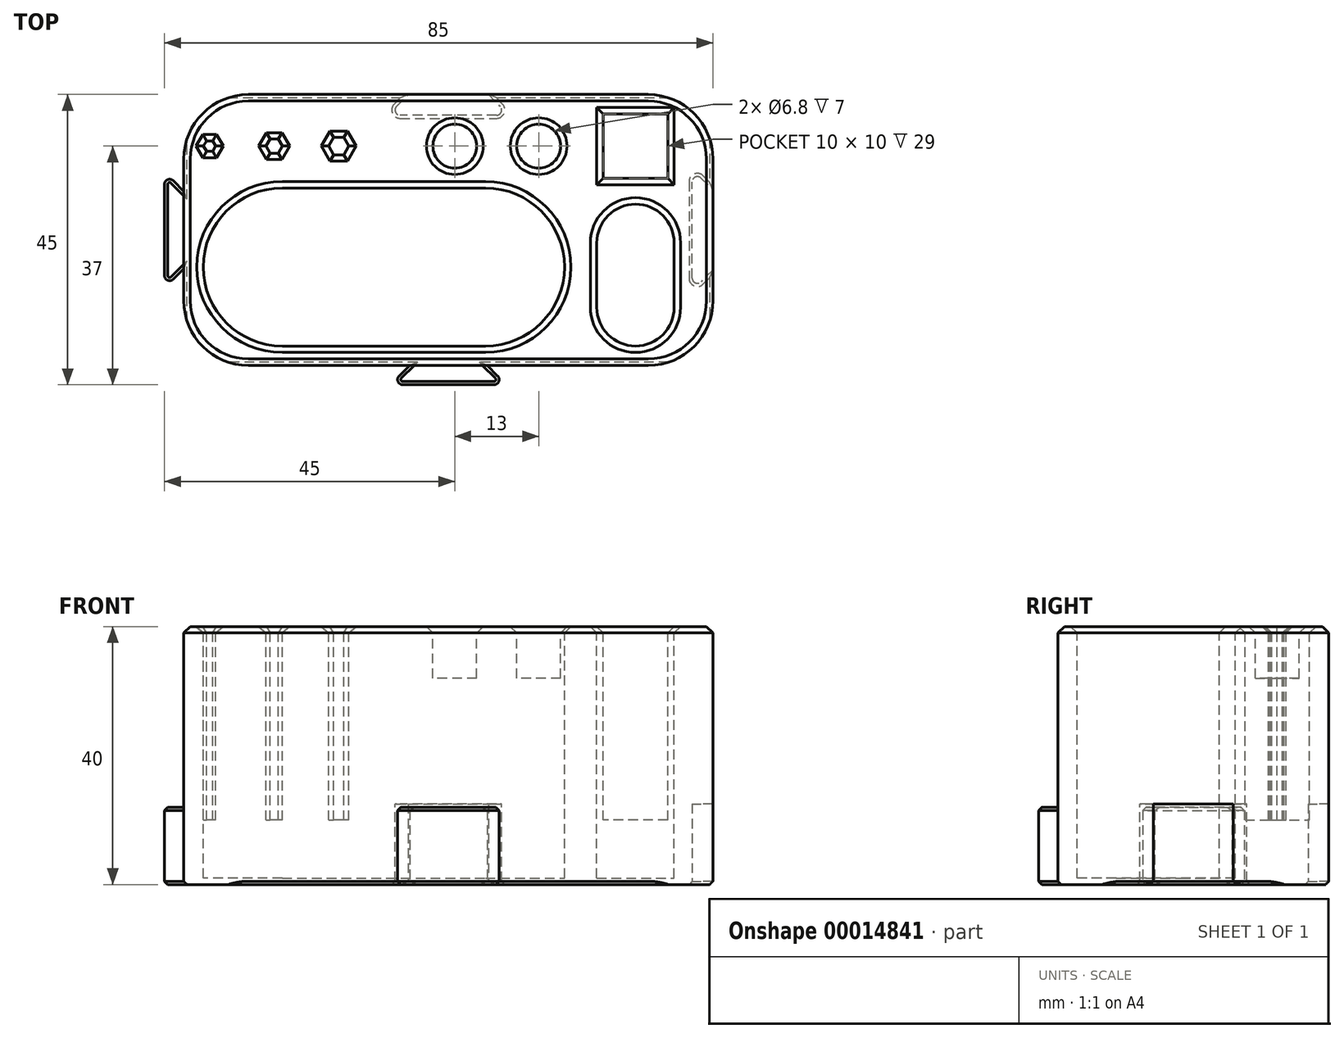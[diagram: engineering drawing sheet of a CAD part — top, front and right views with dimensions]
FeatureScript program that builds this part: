
annotation { "Feature Type Name" : "Feature", "Feature Type Description" : "" }
export const myFeature = defineFeature(function(context is Context, id is Id, definition is map)
    precondition{}
    {
        {
            var Q0;
            Q0=qCreatedBy(makeId("Top.planeOp"),FACE);
            var sketch = newSketch(context, id + "F0", { "sketchPlane" : qUnion([Q0])});
            skLineSegment(sketch, "E0.bottom", {"start": v(0, 0) * mm, "end": v(82, 0) * mm});
            skLineSegment(sketch, "E0.top", {"start": v(0, 42) * mm, "end": v(82, 42) * mm});
            skLineSegment(sketch, "E0.left", {"start": v(0, 0) * mm, "end": v(0, 42) * mm});
            skLineSegment(sketch, "E0.right", {"start": v(82, 0) * mm, "end": v(82, 42) * mm});
            skLineSegment(sketch, "E1", {"start": v(0, 21) * mm, "end": v(82, 21) * mm, "construction": true});
            skLineSegment(sketch, "E2", {"start": v(41, 42) * mm, "end": v(41, 0) * mm, "construction": true});
            skLineSegment(sketch, "E3", {"start": v(35, 0) * mm, "end": v(32, -3) * mm});
            skLineSegment(sketch, "E4", {"start": v(32, -3) * mm, "end": v(50, -3) * mm});
            skLineSegment(sketch, "E5", {"start": v(50, -3) * mm, "end": v(47, 0) * mm});
            skLineSegment(sketch, "E6", {"start": v(47.2, 42) * mm, "end": v(50.4, 38.8) * mm});
            skLineSegment(sketch, "E7", {"start": v(50.4, 38.8) * mm, "end": v(31.6, 38.8) * mm});
            skLineSegment(sketch, "E8", {"start": v(31.6, 38.8) * mm, "end": v(34.8, 42) * mm});
            skLineSegment(sketch, "E9", {"start": v(0, 15) * mm, "end": v(-3, 12) * mm});
            skLineSegment(sketch, "E10", {"start": v(-3, 12) * mm, "end": v(-3, 30) * mm});
            skLineSegment(sketch, "E11", {"start": v(-3, 30) * mm, "end": v(0, 27) * mm});
            skLineSegment(sketch, "E12", {"start": v(82, 14.8) * mm, "end": v(78.8, 11.6) * mm});
            skLineSegment(sketch, "E13", {"start": v(78.8, 11.6) * mm, "end": v(78.8, 30.4) * mm});
            skLineSegment(sketch, "E14", {"start": v(78.8, 30.4) * mm, "end": v(82, 27.2) * mm});
            skSolve(sketch);
        }
        {
            var Q0;
            {var subQ1=sQuery(id+"F0.wireOp",EDGE,"E6");Q0=makeQuery(id+"F0.imprint","IMPRINT",FACE,{"disambiguationData":[TD([[makeQuery(id+"F0.imprint","IMPRINT",EDGE,{"derivedFrom":subQ1}),-1.0]])]});}
            var Q1;
            {var subQ1=sQuery(id+"F0.wireOp",EDGE,"E12");Q1=makeQuery(id+"F0.imprint","IMPRINT",FACE,{"disambiguationData":[TD([[makeQuery(id+"F0.imprint","IMPRINT",EDGE,{"derivedFrom":subQ1}),-1.0]])]});}
            var Q2;
            {var subQ8=sQuery(id+"F0.wireOp",EDGE,"E6");Q2=makeQuery(id+"F0.imprint","IMPRINT",FACE,{"disambiguationData":[TD([[makeQuery(id+"F0.imprint","IMPRINT",EDGE,{"derivedFrom":subQ8}),1.0]])]});}
            extrude(context, id + "F1", {"entities" : qUnion([Q0, Q1, Q2]), "depth" : 40 * mm});
        }
        {
            var Q0;
            {var subQ1=sQuery(id+"F0.wireOp",EDGE,"E3");Q0=makeQuery(id+"F0.imprint","IMPRINT",FACE,{"disambiguationData":[TD([[makeQuery(id+"F0.imprint","IMPRINT",EDGE,{"derivedFrom":subQ1}),1.0]])]});}
            var Q1;
            {var subQ1=sQuery(id+"F0.wireOp",EDGE,"E9");Q1=makeQuery(id+"F0.imprint","IMPRINT",FACE,{"disambiguationData":[TD([[makeQuery(id+"F0.imprint","IMPRINT",EDGE,{"derivedFrom":subQ1}),-1.0]])]});}
            extrude(context, id + "F2", {"entities" : qUnion([Q0, Q1]), "operationType" : NewBodyOperationType.ADD, "depth" : 12 * mm});
        }
        {
            var Q0;
            {var subQ1=sQuery(id+"F0.wireOp",EDGE,"E6");Q0=makeQuery(id+"F0.imprint","IMPRINT",FACE,{"disambiguationData":[TD([[makeQuery(id+"F0.imprint","IMPRINT",EDGE,{"derivedFrom":subQ1}),-1.0]])]});}
            var Q1;
            {var subQ1=sQuery(id+"F0.wireOp",EDGE,"E12");Q1=makeQuery(id+"F0.imprint","IMPRINT",FACE,{"disambiguationData":[TD([[makeQuery(id+"F0.imprint","IMPRINT",EDGE,{"derivedFrom":subQ1}),-1.0]])]});}
            extrude(context, id + "F3", {"entities" : qUnion([Q0, Q1]), "operationType" : NewBodyOperationType.REMOVE, "depth" : 12.5 * mm});
        }
        {
            var Q0;
            Q0=makeQuery(id+"F3.boolean.opBoolean","COPY",EDGE,{"derivedFrom":makeQuery(id+"F3.opExtrude","SWEPT_EDGE",EDGE,{"disambiguationData":[OSD([sQuery(id+"F0.wireOp",EDGE,"E0.right"),sQuery(id+"F0.wireOp",EDGE,"E14")])]})});
            var Q1;
            Q1=makeQuery(id+"F3.boolean.opBoolean","COPY",EDGE,{"derivedFrom":makeQuery(id+"F3.opExtrude","SWEPT_EDGE",EDGE,{"disambiguationData":[OSD([sQuery(id+"F0.wireOp",EDGE,"E13"),sQuery(id+"F0.wireOp",EDGE,"E14")])]})});
            var Q2;
            Q2=makeQuery(id+"F3.boolean.opBoolean","COPY",EDGE,{"derivedFrom":makeQuery(id+"F3.opExtrude","SWEPT_EDGE",EDGE,{"disambiguationData":[OSD([sQuery(id+"F0.wireOp",EDGE,"E0.right"),sQuery(id+"F0.wireOp",EDGE,"E12")])]})});
            var Q3;
            Q3=makeQuery(id+"F2.opExtrude","SWEPT_EDGE",EDGE,{"disambiguationData":[OSD([sQuery(id+"F0.wireOp",EDGE,"E4"),sQuery(id+"F0.wireOp",EDGE,"E5")])]});
            var Q4;
            Q4=makeQuery(id+"F3.boolean.opBoolean","COPY",EDGE,{"derivedFrom":makeQuery(id+"F3.opExtrude","SWEPT_EDGE",EDGE,{"disambiguationData":[OSD([sQuery(id+"F0.wireOp",EDGE,"E12"),sQuery(id+"F0.wireOp",EDGE,"E13")])]})});
            var Q5;
            Q5=makeQuery(id+"F3.boolean.opBoolean","COPY",EDGE,{"derivedFrom":makeQuery(id+"F3.opExtrude","SWEPT_EDGE",EDGE,{"disambiguationData":[OSD([sQuery(id+"F0.wireOp",EDGE,"E0.top"),sQuery(id+"F0.wireOp",EDGE,"E8")])]})});
            var Q6;
            Q6=makeQuery(id+"F3.boolean.opBoolean","COPY",EDGE,{"derivedFrom":makeQuery(id+"F3.opExtrude","SWEPT_EDGE",EDGE,{"disambiguationData":[OSD([sQuery(id+"F0.wireOp",EDGE,"E0.top"),sQuery(id+"F0.wireOp",EDGE,"E6")])]})});
            var Q7;
            Q7=makeQuery(id+"F3.boolean.opBoolean","COPY",EDGE,{"derivedFrom":makeQuery(id+"F3.opExtrude","SWEPT_EDGE",EDGE,{"disambiguationData":[OSD([sQuery(id+"F0.wireOp",EDGE,"E7"),sQuery(id+"F0.wireOp",EDGE,"E8")])]})});
            var Q8;
            Q8=makeQuery(id+"F3.boolean.opBoolean","COPY",EDGE,{"derivedFrom":makeQuery(id+"F3.opExtrude","SWEPT_EDGE",EDGE,{"disambiguationData":[OSD([sQuery(id+"F0.wireOp",EDGE,"E6"),sQuery(id+"F0.wireOp",EDGE,"E7")])]})});
            var Q9;
            Q9=makeQuery(id+"F2.opExtrude","SWEPT_EDGE",EDGE,{"disambiguationData":[OSD([sQuery(id+"F0.wireOp",EDGE,"E10"),sQuery(id+"F0.wireOp",EDGE,"E11")])]});
            var Q10;
            Q10=makeQuery(id+"F2.opExtrude","SWEPT_EDGE",EDGE,{"disambiguationData":[OSD([sQuery(id+"F0.wireOp",EDGE,"E0.left"),sQuery(id+"F0.wireOp",EDGE,"E11")])]});
            var Q11;
            Q11=makeQuery(id+"F2.opExtrude","SWEPT_EDGE",EDGE,{"disambiguationData":[OSD([sQuery(id+"F0.wireOp",EDGE,"E0.left"),sQuery(id+"F0.wireOp",EDGE,"E9")])]});
            var Q12;
            Q12=makeQuery(id+"F2.opExtrude","SWEPT_EDGE",EDGE,{"disambiguationData":[OSD([sQuery(id+"F0.wireOp",EDGE,"E9"),sQuery(id+"F0.wireOp",EDGE,"E10")])]});
            var Q13;
            Q13=makeQuery(id+"F2.opExtrude","SWEPT_EDGE",EDGE,{"disambiguationData":[OSD([sQuery(id+"F0.wireOp",EDGE,"E3"),sQuery(id+"F0.wireOp",EDGE,"E4")])]});
            var Q14;
            Q14=makeQuery(id+"F2.opExtrude","SWEPT_EDGE",EDGE,{"disambiguationData":[OSD([sQuery(id+"F0.wireOp",EDGE,"E0.bottom"),sQuery(id+"F0.wireOp",EDGE,"E3")])]});
            var Q15;
            Q15=makeQuery(id+"F2.opExtrude","SWEPT_EDGE",EDGE,{"disambiguationData":[OSD([sQuery(id+"F0.wireOp",EDGE,"E0.bottom"),sQuery(id+"F0.wireOp",EDGE,"E5")])]});
            fillet(context, id + "F4", {"entities" : qUnion([Q0, Q1, Q2, Q3, Q4, Q5, Q6, Q7, Q8, Q9, Q10, Q11, Q12, Q13, Q14, Q15]), "radius" : .8 * mm, "tangentPropagation" : true, "allowEdgeOverflow" : false});
        }
        {
            var Q0;
            Q0=makeQuery(id+"F2.opExtrude","CAP_EDGE",EDGE,{"disambiguationData":[OSD([sQuery(id+"F0.wireOp",EDGE,"E4")])],"isStart":false});
            var Q1;
            Q1=makeQuery(id+"F2.opExtrude","CAP_EDGE",EDGE,{"disambiguationData":[OSD([sQuery(id+"F0.wireOp",EDGE,"E10")])],"isStart":false});
            chamfer(context, id + "F5", {"entities" : qUnion([Q0, Q1]), "width" : .5 * mm, "tangentPropagation" : true});
        }
        {
            var Q0;
            {var subQ0=sQuery(id+"F0.wireOp",EDGE,"E0.bottom");var subQ1=sQuery(id+"F0.wireOp",EDGE,"E0.left");Q0=makeQuery(id+"F2.boolean.opBoolean","MERGE",FACE,{"derivedFrom":[makeQuery(id+"F1.opExtrude","CAP_FACE",FACE,{"disambiguationData":[OSD([subQ0,sQuery(id+"F0.wireOp",EDGE,"E0.top"),subQ1,sQuery(id+"F0.wireOp",EDGE,"E0.right")])],"isStart":true}),makeQuery(id+"F2.opExtrude","CAP_FACE",FACE,{"disambiguationData":[OSD([subQ0,sQuery(id+"F0.wireOp",EDGE,"E3"),sQuery(id+"F0.wireOp",EDGE,"E4"),sQuery(id+"F0.wireOp",EDGE,"E5")])],"isStart":true}),makeQuery(id+"F2.opExtrude","CAP_FACE",FACE,{"disambiguationData":[OSD([subQ1,sQuery(id+"F0.wireOp",EDGE,"E9"),sQuery(id+"F0.wireOp",EDGE,"E10"),sQuery(id+"F0.wireOp",EDGE,"E11")])],"isStart":true})]});}
            chamfer(context, id + "F6", {"entities" : qUnion([Q0]), "width" : .5 * mm, "tangentPropagation" : true});
        }
        {
            var Q0;
            Q0=makeQuery(id+"F1.opExtrude","CAP_FACE",FACE,{"disambiguationData":[OSD([sQuery(id+"F0.wireOp",EDGE,"E0.bottom"),sQuery(id+"F0.wireOp",EDGE,"E0.top"),sQuery(id+"F0.wireOp",EDGE,"E0.left"),sQuery(id+"F0.wireOp",EDGE,"E0.right")])],"isStart":false});
            var sketch = newSketch(context, id + "F7", { "sketchPlane" : qUnion([Q0])});
            skLineSegment(sketch, "E15", {"start": v(0, 21) * mm, "end": v(82, 21) * mm, "construction": true});
            skLineSegment(sketch, "E16", {"start": v(41, 0) * mm, "end": v(41, 42) * mm, "construction": true});
            skSolve(sketch);
        }
        {
            var Q0;
            Q0=makeQuery(id+"F7.imprint","IMPRINT",FACE,{"disambiguationData":[TD([[makeQuery(id+"F7.imprint","IMPRINT",EDGE,{"derivedFrom":makeQuery(id+"F1.opExtrude","CAP_EDGE",EDGE,{"disambiguationData":[OSD([sQuery(id+"F0.wireOp",EDGE,"E0.bottom")])],"isStart":false})}),1.0]])]});
            var sketch = newSketch(context, id + "F8", { "sketchPlane" : qUnion([Q0])});
            skLineSegment(sketch, "E17", {"start": v(15.25, 27.5) * mm, "end": v(46.75, 27.5) * mm});
            skLineSegment(sketch, "E18", {"start": v(46.75, 3) * mm, "end": v(15.25, 3) * mm});
            skArc(sketch, "E19", {"start": v(15.25, 27.5) * mm, "mid": v(3, 15.25) * mm, "end": v(15.25, 3) * mm});
            skArc(sketch, "E20", {"start": v(46.75, 3) * mm, "mid": v(59, 15.25) * mm, "end": v(46.75, 27.5) * mm});
            skLineSegment(sketch, "E21", {"start": v(76, 19) * mm, "end": v(76, 9) * mm});
            skLineSegment(sketch, "E22", {"start": v(64, 9) * mm, "end": v(64, 19) * mm});
            skArc(sketch, "E23", {"start": v(64, 9) * mm, "mid": v(70, 3) * mm, "end": v(76, 9) * mm});
            skArc(sketch, "E24", {"start": v(76, 19) * mm, "mid": v(70, 25) * mm, "end": v(64, 19) * mm});
            skCircle(sketch, "E25", {"center": v(55, 34) * mm, "radius": 3.4 * mm});
            skLineSegment(sketch, "E26", {"start": v(75, 39) * mm, "end": v(65, 39) * mm});
            skLineSegment(sketch, "E27", {"start": v(65, 39) * mm, "end": v(65, 29) * mm});
            skLineSegment(sketch, "E28", {"start": v(65, 29) * mm, "end": v(75, 29) * mm});
            skLineSegment(sketch, "E29", {"start": v(75, 29) * mm, "end": v(75, 39) * mm});
            skLineSegment(sketch, "E30", {"start": v(65, 34) * mm, "end": v(55, 34) * mm, "construction": true});
            skCircle(sketch, "E31.cCircle", {"center": v(24, 34) * mm, "radius": 1.55 * mm, "construction": true});
            skLineSegment(sketch, "E31.0", {"start": v(22.45, 34) * mm, "end": v(23.23, 35.34) * mm});
            skLineSegment(sketch, "E31.1", {"start": v(23.22, 35.34) * mm, "end": v(24.78, 35.34) * mm});
            skLineSegment(sketch, "E31.2", {"start": v(24.77, 35.34) * mm, "end": v(25.55, 34) * mm});
            skLineSegment(sketch, "E31.3", {"start": v(25.55, 34) * mm, "end": v(24.77, 32.66) * mm});
            skLineSegment(sketch, "E31.4", {"start": v(24.77, 32.66) * mm, "end": v(23.22, 32.66) * mm});
            skLineSegment(sketch, "E31.5", {"start": v(23.23, 32.66) * mm, "end": v(22.45, 34) * mm});
            skCircle(sketch, "E32.cCircle", {"center": v(14, 34) * mm, "radius": 1.25 * mm, "construction": true});
            skLineSegment(sketch, "E32.0", {"start": v(12.75, 34) * mm, "end": v(13.38, 35.08) * mm});
            skLineSegment(sketch, "E32.1", {"start": v(13.37, 35.08) * mm, "end": v(14.63, 35.08) * mm});
            skLineSegment(sketch, "E32.2", {"start": v(14.62, 35.08) * mm, "end": v(15.25, 34) * mm});
            skLineSegment(sketch, "E32.3", {"start": v(15.25, 34) * mm, "end": v(14.63, 32.92) * mm});
            skLineSegment(sketch, "E32.4", {"start": v(14.63, 32.92) * mm, "end": v(13.37, 32.92) * mm});
            skLineSegment(sketch, "E32.5", {"start": v(13.38, 32.92) * mm, "end": v(12.75, 34) * mm});
            skCircle(sketch, "E33.cCircle", {"center": v(4, 34) * mm, "radius": 0.95 * mm, "construction": true});
            skLineSegment(sketch, "E33.0", {"start": v(3.05, 34) * mm, "end": v(3.52, 34.82) * mm});
            skLineSegment(sketch, "E33.1", {"start": v(3.52, 34.82) * mm, "end": v(4.47, 34.82) * mm});
            skLineSegment(sketch, "E33.2", {"start": v(4.47, 34.82) * mm, "end": v(4.95, 34) * mm});
            skLineSegment(sketch, "E33.3", {"start": v(4.95, 34) * mm, "end": v(4.48, 33.18) * mm});
            skLineSegment(sketch, "E33.4", {"start": v(4.48, 33.18) * mm, "end": v(3.53, 33.18) * mm});
            skLineSegment(sketch, "E33.5", {"start": v(3.52, 33.18) * mm, "end": v(3.05, 34) * mm});
            skLineSegment(sketch, "E34", {"start": v(4, 34) * mm, "end": v(14, 34) * mm, "construction": true});
            skLineSegment(sketch, "E35", {"start": v(24, 34) * mm, "end": v(14, 34) * mm, "construction": true});
            skLineSegment(sketch, "E36", {"start": v(24, 34) * mm, "end": v(55, 34) * mm, "construction": true});
            skLineSegment(sketch, "E37", {"start": v(70, 19) * mm, "end": v(70, 29) * mm, "construction": true});
            skCircle(sketch, "E38", {"center": v(42, 34) * mm, "radius": 3.4 * mm});
            skCircle(sketch, "E39", {"center": v(32.54, 34) * mm, "radius": 2.14 * mm});
            skSolve(sketch);
        }
        {
            var Q0;
            Q0=makeQuery(id+"F8.imprint","IMPRINT",FACE,{"disambiguationData":[TD([[makeQuery(id+"F8.imprint","IMPRINT",EDGE,{"derivedFrom":sQuery(id+"F8.wireOp",EDGE,"E26")}),1.0]])]});
            extrude(context, id + "F9", {"entities" : qUnion([Q0]), "operationType" : NewBodyOperationType.REMOVE, "oppositeDirection" : true, "depth" : 30 * mm});
        }
        {
            var Q0;
            Q0=makeQuery(id+"F8.imprint","IMPRINT",FACE,{"disambiguationData":[TD([[makeQuery(id+"F8.imprint","IMPRINT",EDGE,{"derivedFrom":sQuery(id+"F8.wireOp",EDGE,"E17")}),-1.0]])]});
            var Q1;
            Q1=makeQuery(id+"F8.imprint","IMPRINT",FACE,{"disambiguationData":[TD([[makeQuery(id+"F8.imprint","IMPRINT",EDGE,{"derivedFrom":sQuery(id+"F8.wireOp",EDGE,"E21")}),-1.0]])]});
            extrude(context, id + "F10", {"entities" : qUnion([Q0, Q1]), "operationType" : NewBodyOperationType.REMOVE, "oppositeDirection" : true, "depth" : 39 * mm});
        }
        {
            var Q0;
            Q0=makeQuery(id+"F8.imprint","IMPRINT",FACE,{"disambiguationData":[TD([[makeQuery(id+"F8.imprint","IMPRINT",EDGE,{"derivedFrom":sQuery(id+"F8.wireOp",EDGE,"E25")}),1.0]])]});
            var Q1;
            Q1=makeQuery(id+"F8.imprint","IMPRINT",FACE,{"disambiguationData":[TD([[makeQuery(id+"F8.imprint","IMPRINT",EDGE,{"derivedFrom":sQuery(id+"F8.wireOp",EDGE,"E38")}),1.0]])]});
            extrude(context, id + "F11", {"entities" : qUnion([Q0, Q1]), "operationType" : NewBodyOperationType.REMOVE, "oppositeDirection" : true, "depth" : 8 * mm});
        }
        {
            var Q0;
            Q0=makeQuery(id+"F8.imprint","IMPRINT",FACE,{"disambiguationData":[TD([[makeQuery(id+"F8.imprint","IMPRINT",EDGE,{"derivedFrom":sQuery(id+"F8.wireOp",EDGE,"E31.0")}),-1.0]])]});
            var Q1;
            Q1=makeQuery(id+"F8.imprint","IMPRINT",FACE,{"disambiguationData":[TD([[makeQuery(id+"F8.imprint","IMPRINT",EDGE,{"derivedFrom":sQuery(id+"F8.wireOp",EDGE,"E32.0")}),-1.0]])]});
            var Q2;
            Q2=makeQuery(id+"F8.imprint","IMPRINT",FACE,{"disambiguationData":[TD([[makeQuery(id+"F8.imprint","IMPRINT",EDGE,{"derivedFrom":sQuery(id+"F8.wireOp",EDGE,"E33.0")}),-1.0]])]});
            extrude(context, id + "F12", {"entities" : qUnion([Q0, Q1, Q2]), "operationType" : NewBodyOperationType.REMOVE, "oppositeDirection" : true, "depth" : 30 * mm});
        }
        {
            var Q0;
            Q0=makeQuery(id+"F1.opExtrude","SWEPT_EDGE",EDGE,{"disambiguationData":[OSD([sQuery(id+"F0.wireOp",EDGE,"E0.bottom"),sQuery(id+"F0.wireOp",EDGE,"E0.left")])]});
            var Q1;
            Q1=makeQuery(id+"F1.opExtrude","SWEPT_EDGE",EDGE,{"disambiguationData":[OSD([sQuery(id+"F0.wireOp",EDGE,"E0.bottom"),sQuery(id+"F0.wireOp",EDGE,"E0.right")])]});
            var Q2;
            Q2=makeQuery(id+"F1.opExtrude","SWEPT_EDGE",EDGE,{"disambiguationData":[OSD([sQuery(id+"F0.wireOp",EDGE,"E0.top"),sQuery(id+"F0.wireOp",EDGE,"E0.right")])]});
            var Q3;
            Q3=makeQuery(id+"F1.opExtrude","SWEPT_EDGE",EDGE,{"disambiguationData":[OSD([sQuery(id+"F0.wireOp",EDGE,"E0.top"),sQuery(id+"F0.wireOp",EDGE,"E0.left")])]});
            fillet(context, id + "F13", {"entities" : qUnion([Q0, Q1, Q2, Q3]), "radius" : 10 * mm, "tangentPropagation" : true, "allowEdgeOverflow" : false});
        }
        {
            var Q0;
            Q0=makeQuery(id+"F1.opExtrude","CAP_FACE",FACE,{"disambiguationData":[OSD([sQuery(id+"F0.wireOp",EDGE,"E0.bottom"),sQuery(id+"F0.wireOp",EDGE,"E0.top"),sQuery(id+"F0.wireOp",EDGE,"E0.left"),sQuery(id+"F0.wireOp",EDGE,"E0.right")])],"isStart":false});
            chamfer(context, id + "F14", {"entities" : qUnion([Q0]), "width" : 1 * mm, "tangentPropagation" : true});
        }
    });
